FCSTD DOCUMENT  (FreeCAD 0.14R3702 (Git))
Label: flipped_right_side_plate
License: CC-BY 3.0
LicenseURL: http://creativecommons.org/licenses/by/3.0/
objects: Part::Feature×34, Mesh::Feature×23, Part::Cylinder×15, Sketcher::SketchObject×4, PartDesign::Pocket×4, Part::Box×2
note: 63 computed .brp shape members not serialized (recipe doc carries the construction recipe); baked Part::Feature solids carry a one-line shape summary decoded from their .brp

FEATURE [Part::Cylinder] Cylinder  label="left_back_rod"
  Angle = 360
  Height = 1200
  Placement = pos=(-480,-780,-10) rot=(0,0,1;0rad)
  Radius = 4
FEATURE [Part::Cylinder] Cylinder001  label="right_back_rod"
  Angle = 360
  Height = 1200
  Placement = pos=(480,-780,-10) rot=(0,0,1;0rad)
  Radius = 4
FEATURE [Part::Cylinder] Cylinder002  label="right_front_rod"
  Angle = 360
  Height = 1200
  Placement = pos=(480,-938,-10) rot=(0,0,1;0rad)
  Radius = 4
FEATURE [Part::Cylinder] Cylinder003  label="left_front_rod"
  Angle = 360
  Height = 1200
  Placement = pos=(-480,-938,-10) rot=(0,0,-1;1.5708rad)
  Radius = 4
FEATURE [Part::Feature] Part__Feature023  label="left_stepper_motor"
  Placement = pos=(-471,-867,-13) rot=(0,0,1;0rad)
  shape: bbox 48 x 42.3 x 60.1 mm, 110 faces (baked)
FEATURE [Part::Feature] Part__Feature025  label="right_stepper_motor"
  Placement = pos=(471,-867,-13) rot=(0,0,1;0rad)
  shape: bbox 48 x 42.3 x 60.1 mm, 110 faces (baked)
FEATURE [Part::Feature] Part__Feature027  label="left_front_bottom_guide"
  Placement = pos=(-500,-938,-5) rot=(0,0,-1;1.5708rad)
  shape: bbox 32.8 x 42 x 14 mm, 11 faces (baked)
FEATURE [Part::Feature] Part__Feature028  label="left_front_top_guide"
  Placement = pos=(-500,-938,1045) rot=(0,0,-1;1.5708rad)
  shape: bbox 32.8 x 42 x 14 mm, 11 faces (baked)
FEATURE [Part::Feature] Part__Feature029  label="left_back_top_guide"
  Placement = pos=(-500,-780,1045) rot=(0,0,-1;1.5708rad)
  shape: bbox 32.8 x 42 x 14 mm, 11 faces (baked)
FEATURE [Part::Feature] Part__Feature030  label="left_back_bottom_guide"
  Placement = pos=(-500,-780,-5) rot=(0,0,-1;1.5708rad)
  shape: bbox 32.8 x 42 x 14 mm, 11 faces (baked)
FEATURE [Part::Feature] Part__Feature031  label="right_back_bottom_guide"
  Placement = pos=(500,-780,-5) rot=(0,0,1;1.5708rad)
  shape: bbox 32.8 x 42 x 14 mm, 11 faces (baked)
FEATURE [Part::Feature] Part__Feature032  label="right_front_bottom_guide"
  Placement = pos=(500,-938,-5) rot=(0,0,1;1.5708rad)
  shape: bbox 32.8 x 42 x 14 mm, 11 faces (baked)
FEATURE [Part::Feature] Part__Feature033  label="right_front_top_guide"
  Placement = pos=(500,-938,1045) rot=(0,0,1;1.5708rad)
  shape: bbox 32.8 x 42 x 14 mm, 11 faces (baked)
FEATURE [Part::Feature] Part__Feature034  label="right_back_top_guide"
  Placement = pos=(500,-780,1045) rot=(0,0,1;1.5708rad)
  shape: bbox 32.8 x 42 x 14 mm, 11 faces (baked)
FEATURE [Part::Feature] Part__Feature036  label="left_front_foot"
  Placement = pos=(-510,-975,-45) rot=(0,0,1;0rad)
  shape: bbox 34.53 x 34.53 x 32.52 mm, 61 faces (baked)
FEATURE [Part::Feature] Part__Feature037  label="left_back_foot"
  Placement = pos=(-510,10,-45) rot=(0,0,1;0rad)
  shape: bbox 34.53 x 34.53 x 32.52 mm, 61 faces (baked)
FEATURE [Part::Feature] Part__Feature038  label="right_back_foot"
  Placement = pos=(512,3,-45) rot=(0,0,1;0rad)
  shape: bbox 34.53 x 34.53 x 32.52 mm, 61 faces (baked)
FEATURE [Part::Feature] Part__Feature039  label="right_front_foot"
  Placement = pos=(510,-973,-45) rot=(0,0,1;0rad)
  shape: bbox 34.53 x 34.53 x 32.52 mm, 61 faces (baked)
FEATURE [Part::Cylinder] Cylinder004  label="left_lead_screw"
  Angle = 360
  Height = 1066.8
  Placement = pos=(-482,-836,778) rot=(0,1,0;1.5708rad)
  Radius = 5.556
FEATURE [Part::Cylinder] Cylinder005  label="right_lead_screw"
  Angle = 360
  Height = 1219.2
  Placement = pos=(472,-866,55) rot=(0,0,1;0rad)
  Radius = 4.7625
FEATURE [Part::Cylinder] Cylinder006  label="front_rail_guide_rod"
  Angle = 360
  Height = 1000
  Placement = pos=(-500,-913,800) rot=(0,1,0;1.5708rad)
  Radius = 10
FEATURE [Part::Cylinder] Cylinder007  label="back_rail_guide_rod"
  Angle = 360
  Height = 1000
  Placement = pos=(-500,-805,800) rot=(0,1,0;1.5708rad)
  Radius = 10
FEATURE [Part::Feature] Part__Feature046  label="back_bottom_rail"
  Placement = pos=(-500,0,25) rot=(0,1,0;1.5708rad)
  shape: bbox 1000 x 24.5 x 25 mm, 50 faces (baked)
FEATURE [Part::Feature] Part__Feature047  label="rail"
  Placement = pos=(512.5,0,37.5) rot=(0,0,1;0rad)
  shape: bbox 25 x 24.5 x 1000 mm, 50 faces (baked)
FEATURE [Part::Feature] Part__Feature  label="rail001"
  Placement = pos=(512.5,12.5,0) rot=(1,0,0;1.5708rad)
  shape: bbox 25 x 1000 x 24.5 mm, 50 faces (baked)
FEATURE [Part::Feature] Part__Feature048  label="rail002"
  Placement = pos=(512.5,12.5,25) rot=(1,0,0;1.5708rad)
  shape: bbox 25 x 1000 x 24.5 mm, 50 faces (baked)
FEATURE [Part::Feature] Part__Feature049  label="rail003"
  Placement = pos=(-512.5,0,37.5) rot=(0,0,1;0rad)
  shape: bbox 25 x 24.5 x 1000 mm, 50 faces (baked)
FEATURE [Part::Feature] Part__Feature050  label="back_bottom_rail001"
  Placement = pos=(-500,0,1050) rot=(0,1,0;1.5708rad)
  shape: bbox 1000 x 24.5 x 25 mm, 50 faces (baked)
FEATURE [Part::Feature] Part__Feature051  label="back_bottom_rail002"
  Placement = pos=(-500,-975,25) rot=(0,1,0;1.5708rad)
  shape: bbox 1000 x 24.5 x 25 mm, 50 faces (baked)
FEATURE [Part::Feature] Part__Feature052  label="back_bottom_rail003"
  Placement = pos=(-500,-725,1050) rot=(0,1,0;1.5708rad)
  shape: bbox 1000 x 24.5 x 25 mm, 50 faces (baked)
FEATURE [Part::Feature] Part__Feature053  label="rail004"
  Placement = pos=(512.5,12.5,1050) rot=(1,0,0;1.5708rad)
  shape: bbox 25 x 1000 x 24.5 mm, 50 faces (baked)
FEATURE [Part::Feature] Part__Feature054  label="rail005"
  Placement = pos=(512.5,-975,37.5) rot=(0,0,1;0rad)
  shape: bbox 25 x 24.5 x 1000 mm, 50 faces (baked)
FEATURE [Part::Feature] Part__Feature055  label="rail006"
  Placement = pos=(512.5,-725,37.5) rot=(0,0,1;0rad)
  shape: bbox 25 x 24.5 x 1000 mm, 50 faces (baked)
FEATURE [Part::Feature] Part__Feature056  label="rail007"
  Placement = pos=(-512.5,12.5,25) rot=(1,0,0;1.5708rad)
  shape: bbox 25 x 1000 x 24.5 mm, 50 faces (baked)
FEATURE [Part::Feature] Part__Feature057  label="rail008"
  Placement = pos=(-512.5,12.5,0) rot=(1,0,0;1.5708rad)
  shape: bbox 25 x 1000 x 24.5 mm, 50 faces (baked)
FEATURE [Part::Feature] Part__Feature058  label="rail009"
  Placement = pos=(-512.5,12.5,1050) rot=(1,0,0;1.5708rad)
  shape: bbox 25 x 1000 x 24.5 mm, 50 faces (baked)
FEATURE [Part::Feature] Part__Feature059  label="rail010"
  Placement = pos=(-512.5,-725,37.5) rot=(0,0,1;0rad)
  shape: bbox 25 x 24.5 x 1000 mm, 50 faces (baked)
FEATURE [Part::Feature] Part__Feature060  label="rail011"
  Placement = pos=(-512.5,-975,37.5) rot=(0,0,1;0rad)
  shape: bbox 25 x 24.5 x 1000 mm, 50 faces (baked)
FEATURE [Part::Feature] Part__Feature061  label="1"
  Placement = pos=(-472,-867,52) rot=(0,1,0;1.5708rad)
  shape: bbox 20 x 20 x 28 mm, 505 faces (baked)
FEATURE [Part::Feature] Part__Feature062  label="002"
  Placement = pos=(470,-867,52) rot=(0,1,0;1.5708rad)
  shape: bbox 20 x 20 x 28 mm, 505 faces (baked)
FEATURE [Part::Cylinder] Cylinder008  label="Cylinder"
  Angle = 360
  Height = 7
  Placement = pos=(-471,-866,80) rot=(0,0,1;0rad)
  Radius = 11
FEATURE [Part::Cylinder] Cylinder010  label="x-axis-bearing-left"
  Angle = 360
  Height = 9
  Placement = pos=(-453,-836,778) rot=(0,1,0;1.5708rad)
  Radius = 15
FEATURE [Part::Cylinder] Cylinder012  label="left_lead_screw001"
  Angle = 360
  Height = 1219.2
  Placement = pos=(-472,-866,55) rot=(0,0,1;0rad)
  Radius = 4.7625
FEATURE [Part::Cylinder] Cylinder014  label="x-axis-bearing-right"
  Angle = 360
  Height = 9
  Placement = pos=(466,-836,778) rot=(0,1,0;1.5708rad)
  Radius = 15
FEATURE [Part::Cylinder] Cylinder015  label="Cylinder006"
  Angle = 360
  Height = 7
  Placement = pos=(471,-866,80) rot=(0,0,1;0rad)
  Radius = 11
FEATURE [Part::Cylinder] Cylinder016  label="Cylinder007"
  Angle = 360
  Height = 7
  Placement = pos=(471,-866,1053) rot=(0,0,1;0rad)
  Radius = 11
FEATURE [Part::Cylinder] Cylinder017  label="Cylinder008"
  Angle = 360
  Height = 7
  Placement = pos=(-471,-866,1053) rot=(0,0,1;0rad)
  Radius = 11
FEATURE [Part::Feature] Part__Feature063  label="003"
  Placement = pos=(-477,-835,779) rot=(0,0,1;0rad)
  shape: bbox 28 x 20 x 20 mm, 505 faces (baked)
FEATURE [Part::Feature] Part__Feature064  label="x_axis_stepper_motor"
  Placement = pos=(-541,-835,779) rot=(0,1,0;1.5708rad)
  shape: bbox 60.1 x 42.3 x 48 mm, 110 faces (baked)
FEATURE [Mesh::Feature] top_bearing_mount_lr  label="top_bearing_mount_left"
  Placement = pos=(-494,-826,1062.5) rot=(0.707107,-0.707107,0;3.14159rad)
FEATURE [Mesh::Feature] top_bearing_mount_lr001  label="top_bearing_mount_right"
  Placement = pos=(494,-906,1062.5) rot=(0.707107,0.707107,0;3.14159rad)
FEATURE [Sketcher::SketchObject] Sketch
  Placement = pos=(-453,-836,778) rot=(0.707107,0,-0.707107;3.14159rad)
  Support = -> Cylinder010 [Face3]
  sketch-geometry (1):
    g0: Circle CenterX=0 CenterY=0 CenterZ=0 NormalX=0 NormalY=0 NormalZ=1 Radius=5
  constraints (2):
    c: Coincident(g0,g-1)
    c: Radius(g0) = 5
FEATURE [PartDesign::Pocket] Pocket
  Length = 5
  Placement = pos=(-453,-836,778) rot=(0,1,0;1.5708rad)
  Sketch = -> Sketch
  Type = 1
FEATURE [Sketcher::SketchObject] Sketch001
  Placement = pos=(466,-836,778) rot=(0.707107,0,-0.707107;3.14159rad)
  Support = -> Cylinder014 [Face3]
  sketch-geometry (1):
    g0: Circle CenterX=0 CenterY=0 CenterZ=0 NormalX=0 NormalY=0 NormalZ=1 Radius=5
  constraints (2):
    c: Radius(g0) = 5
    c: Coincident(g0,g-1)
FEATURE [PartDesign::Pocket] Pocket001
  Length = 5
  Placement = pos=(466,-836,778) rot=(0,1,0;1.5708rad)
  Sketch = -> Sketch001
  Type = 1
FEATURE [Part::Box] Box  label="left_slide_rail_plate"
  Height = 80
  Length = 6
  Placement = pos=(493,-958,759) rot=(0,0,1;0rad)
  Width = 200
FEATURE [Mesh::Feature] lm8uu_bearing
  Placement = pos=(480,-780,760) rot=(0,0,1;0rad)
FEATURE [Sketcher::SketchObject] Sketch002
  Placement = pos=(499,-958,759) rot=(0.57735,0.57735,0.57735;2.0944rad)
  Support = -> Box [Face2]
  sketch-geometry (24):
    g0: Circle CenterX=45 CenterY=41 CenterZ=0 NormalX=0 NormalY=0 NormalZ=1 Radius=10
    g1: Circle CenterX=153 CenterY=41 CenterZ=0 NormalX=0 NormalY=0 NormalZ=1 Radius=10
    g2: Circle CenterX=122 CenterY=19 CenterZ=0 NormalX=0 NormalY=0 NormalZ=1 Radius=10
    g3: Circle CenterX=36.5 CenterY=74 CenterZ=0 NormalX=0 NormalY=0 NormalZ=1 Radius=2.5
    g4: Circle CenterX=36.5 CenterY=60 CenterZ=0 NormalX=0 NormalY=0 NormalZ=1 Radius=2.5
    g5: Circle CenterX=5.5 CenterY=74 CenterZ=0 NormalX=0 NormalY=0 NormalZ=1 Radius=2.5
    g6: Circle CenterX=5.5 CenterY=60 CenterZ=0 NormalX=0 NormalY=0 NormalZ=1 Radius=2.5
    g7: Circle CenterX=37 CenterY=19.5 CenterZ=0 NormalX=0 NormalY=0 NormalZ=1 Radius=2.5
    g8: Circle CenterX=37 CenterY=5.5 CenterZ=0 NormalX=0 NormalY=0 NormalZ=1 Radius=2.5
    g9: Circle CenterX=5.5 CenterY=19.5 CenterZ=0 NormalX=0 NormalY=0 NormalZ=1 Radius=2.5
    g10: Circle CenterX=5.5 CenterY=5.5 CenterZ=0 NormalX=0 NormalY=0 NormalZ=1 Radius=2.5
    g11: Circle CenterX=162.5 CenterY=19.5 CenterZ=0 NormalX=0 NormalY=0 NormalZ=1 Radius=2.5
    g12: Circle CenterX=162.5 CenterY=5.5 CenterZ=0 NormalX=0 NormalY=0 NormalZ=1 Radius=2.5
    g13: Circle CenterX=194 CenterY=19.5 CenterZ=0 NormalX=0 NormalY=0 NormalZ=1 Radius=2.5
    g14: Circle CenterX=194 CenterY=5.5 CenterZ=0 NormalX=0 NormalY=0 NormalZ=1 Radius=2.5
    g15: Circle CenterX=162.5 CenterY=74 CenterZ=0 NormalX=0 NormalY=0 NormalZ=1 Radius=2.5
    g16: Circle CenterX=162.5 CenterY=60 CenterZ=0 NormalX=0 NormalY=0 NormalZ=1 Radius=2.5
    g17: Circle CenterX=194 CenterY=74 CenterZ=0 NormalX=0 NormalY=0 NormalZ=1 Radius=2.5
    g18: Circle CenterX=194 CenterY=60 CenterZ=0 NormalX=0 NormalY=0 NormalZ=1 Radius=2.5
    g19: Circle CenterX=107 CenterY=34 CenterZ=0 NormalX=0 NormalY=0 NormalZ=1 Radius=2.5
    g20: Circle CenterX=135 CenterY=36 CenterZ=0 NormalX=0 NormalY=0 NormalZ=1 Radius=2.5
    g21: Circle CenterX=142 CenterY=10 CenterZ=0 NormalX=0 NormalY=0 NormalZ=1 Radius=2.5
    g22: Circle CenterX=77 CenterY=34 CenterZ=0 NormalX=0 NormalY=0 NormalZ=1 Radius=2.5
    g23: Circle CenterX=77 CenterY=14 CenterZ=0 NormalX=0 NormalY=0 NormalZ=1 Radius=2.5
  constraints (68):
    c: Radius(g0) = 10
    c: DistanceX(g-1,g0) = 45
    c: DistanceY(g-1,g0) = 41
    c: Radius(g1) = 10
    c: DistanceX(g-1,g1) = 153
    c: DistanceY(g-1,g1) = 41
    c: Radius(g2) = 10
    c: DistanceX(g-1,g2) = 122
    c: DistanceY(g-1,g2) = 19
    c: Radius(g3) = 2.5
    c: DistanceX(g-1,g3) = 36.5
    c: Equal(g4,g3)
    c: DistanceX(g-1,g4) = 36.5
    c: DistanceY(g-1,g4) = 60
    c: Equal(g4,g5)
    c: DistanceX(g5) = 5.5
    c: DistanceX(g6) = 5.5
    c: DistanceY(g-1,g6) = 60
    c: Equal(g5,g6)
    c: Equal(g6,g9)
    c: Equal(g9,g10)
    c: Equal(g10,g7)
    c: Equal(g7,g8)
    c: Equal(g8,g22)
    c: Equal(g22,g23)
    c: Equal(g23,g19)
    c: Equal(g20,g21)
    c: Equal(g21,g11)
    c: Equal(g11,g12)
    c: Equal(g12,g15)
    c: Equal(g15,g16)
    c: Equal(g16,g17)
    c: Equal(g17,g18)
    c: Equal(g18,g13)
    c: Equal(g13,g14)
    c: DistanceX(g-1,g9) = 5.5
    c: DistanceX(g-1,g10) = 5.5
    c: DistanceX(g7,g9) = -31.5
    c: DistanceX(g8,g10) = -31.5
    c: DistanceY(g9,g10) = -14
    c: DistanceY(g7,g8) = -14
    c: DistanceY(g-1,g8) = 5.5
    c: DistanceY(g-1,g10) = 5.5
    c: DistanceY(g12,g11) = 14
    c: DistanceY(g13,g14) = -14
    c: DistanceY(g-1,g12) = 5.5
    c: DistanceY(g-1,g14) = 5.5
    c: DistanceX(g-1,g11) = 162.5
    c: DistanceX(g-1,g12) = 162.5
    c: DistanceX(g12,g14) = 31.5
    c: DistanceX(g11,g13) = 31.5
    c: DistanceY(g16,g15) = 14
    c: DistanceY(g17,g18) = -14
    c: DistanceX(g16,g18) = 31.5
    c: DistanceX(g15,g17) = 31.5
    c: DistanceX(g-1,g16) = 162.5
    c: DistanceX(g-1,g15) = 162.5
    c: DistanceY(g-1,g16) = 60
    c: DistanceY(g-1,g18) = 60
    c: DistanceY(g-1,g21) = 10
    c: DistanceX(g-1,g21) = 142
    c: DistanceX(g-1,g20) = 135
    c: DistanceY(g21,g20) = 26
    c: DistanceX(g-1,g19) = 107
    c: DistanceY(g-1,g23) = 14
    c: DistanceY(g23,g22) = 20
    c: DistanceX(g19,g22) = -30
    c: DistanceY(g-1,g19) = 34
FEATURE [Mesh::Feature] lm8uu_bearing001
  Placement = pos=(480,-780,813) rot=(0,0,1;0rad)
FEATURE [Mesh::Feature] lm8uu_bearing002
  Placement = pos=(480,-938,760) rot=(0,0,1;0rad)
FEATURE [Mesh::Feature] lm8uu_bearing003
  Placement = pos=(480,-938,814) rot=(0,0,1;0rad)
FEATURE [PartDesign::Pocket] Pocket002
  Length = 5
  Placement = pos=(493,-958,759) rot=(0,0,1;0rad)
  Sketch = -> Sketch002
  Type = 1
FEATURE [Mesh::Feature] lead_screw_flange  label="x-axis-lead-screw-flange"
  Placement = pos=(0,-836,778) rot=(0,1,0;1.5708rad)
FEATURE [Mesh::Feature] lead_screw_flange001  label="z-axis-lead-screw-flange-right"
  Placement = pos=(472,-866,721) rot=(0,0,1;0rad)
FEATURE [Mesh::Feature] lead_screw_flange002  label="z-axis-lead-screw-flange-left"
  Placement = pos=(-472,-866,721) rot=(0,0,-1;0.523599rad)
FEATURE [Part::Box] Box001  label="Cube001"
  Height = 80
  Length = 6
  Placement = pos=(-460,-958,759) rot=(0,0,1;0rad)
  Width = 200
FEATURE [Sketcher::SketchObject] Sketch003
  Placement = pos=(-454,-958,759) rot=(0.57735,0.57735,0.57735;2.0944rad)
  Support = -> Box001 [Face2]
  sketch-geometry (24):
    g0: Circle CenterX=45 CenterY=41 CenterZ=0 NormalX=0 NormalY=0 NormalZ=1 Radius=10
    g1: Circle CenterX=153 CenterY=41 CenterZ=0 NormalX=0 NormalY=0 NormalZ=1 Radius=10
    g2: Circle CenterX=122 CenterY=19 CenterZ=0 NormalX=0 NormalY=0 NormalZ=1 Radius=10
    g3: Circle CenterX=36.5 CenterY=74 CenterZ=0 NormalX=0 NormalY=0 NormalZ=1 Radius=2.5
    g4: Circle CenterX=36.5 CenterY=60 CenterZ=0 NormalX=0 NormalY=0 NormalZ=1 Radius=2.5
    g5: Circle CenterX=5.5 CenterY=74 CenterZ=0 NormalX=0 NormalY=0 NormalZ=1 Radius=2.5
    g6: Circle CenterX=5.5 CenterY=60 CenterZ=0 NormalX=0 NormalY=0 NormalZ=1 Radius=2.5
    g7: Circle CenterX=37 CenterY=19.5 CenterZ=0 NormalX=0 NormalY=0 NormalZ=1 Radius=2.5
    g8: Circle CenterX=37 CenterY=5.5 CenterZ=0 NormalX=0 NormalY=0 NormalZ=1 Radius=2.5
    g9: Circle CenterX=5.5 CenterY=19.5 CenterZ=0 NormalX=0 NormalY=0 NormalZ=1 Radius=2.5
    g10: Circle CenterX=5.5 CenterY=5.5 CenterZ=0 NormalX=0 NormalY=0 NormalZ=1 Radius=2.5
    g11: Circle CenterX=162.5 CenterY=19.5 CenterZ=0 NormalX=0 NormalY=0 NormalZ=1 Radius=2.5
    g12: Circle CenterX=162.5 CenterY=5.5 CenterZ=0 NormalX=0 NormalY=0 NormalZ=1 Radius=2.5
    g13: Circle CenterX=194 CenterY=19.5 CenterZ=0 NormalX=0 NormalY=0 NormalZ=1 Radius=2.5
    g14: Circle CenterX=194 CenterY=5.5 CenterZ=0 NormalX=0 NormalY=0 NormalZ=1 Radius=2.5
    g15: Circle CenterX=162.5 CenterY=74 CenterZ=0 NormalX=0 NormalY=0 NormalZ=1 Radius=2.5
    g16: Circle CenterX=162.5 CenterY=60 CenterZ=0 NormalX=0 NormalY=0 NormalZ=1 Radius=2.5
    g17: Circle CenterX=194 CenterY=74 CenterZ=0 NormalX=0 NormalY=0 NormalZ=1 Radius=2.5
    g18: Circle CenterX=194 CenterY=60 CenterZ=0 NormalX=0 NormalY=0 NormalZ=1 Radius=2.5
    g19: Circle CenterX=107 CenterY=34 CenterZ=0 NormalX=0 NormalY=0 NormalZ=1 Radius=2.5
    g20: Circle CenterX=135 CenterY=36 CenterZ=0 NormalX=0 NormalY=0 NormalZ=1 Radius=2.5
    g21: Circle CenterX=142 CenterY=10 CenterZ=0 NormalX=0 NormalY=0 NormalZ=1 Radius=2.5
    g22: Circle CenterX=77 CenterY=34 CenterZ=0 NormalX=0 NormalY=0 NormalZ=1 Radius=2.5
    g23: Circle CenterX=77 CenterY=14 CenterZ=0 NormalX=0 NormalY=0 NormalZ=1 Radius=2.5
  constraints (68):
    c: Radius(g0) = 10
    c: DistanceX(g-1,g0) = 45
    c: DistanceY(g-1,g0) = 41
    c: Radius(g1) = 10
    c: DistanceX(g-1,g1) = 153
    c: DistanceY(g-1,g1) = 41
    c: Radius(g2) = 10
    c: DistanceX(g-1,g2) = 122
    c: DistanceY(g-1,g2) = 19
    c: Radius(g3) = 2.5
    c: DistanceX(g-1,g3) = 36.5
    c: Equal(g4,g3)
    c: DistanceX(g-1,g4) = 36.5
    c: DistanceY(g-1,g4) = 60
    c: Equal(g4,g5)
    c: DistanceX(g5) = 5.5
    c: DistanceX(g6) = 5.5
    c: DistanceY(g-1,g6) = 60
    c: Equal(g5,g6)
    c: Equal(g6,g9)
    c: Equal(g9,g10)
    c: Equal(g10,g7)
    c: Equal(g7,g8)
    c: Equal(g8,g22)
    c: Equal(g22,g23)
    c: Equal(g23,g19)
    c: Equal(g20,g21)
    c: Equal(g21,g11)
    c: Equal(g11,g12)
    c: Equal(g12,g15)
    c: Equal(g15,g16)
    c: Equal(g16,g17)
    c: Equal(g17,g18)
    c: Equal(g18,g13)
    c: Equal(g13,g14)
    c: DistanceX(g-1,g9) = 5.5
    c: DistanceX(g-1,g10) = 5.5
    c: DistanceX(g7,g9) = -31.5
    c: DistanceX(g8,g10) = -31.5
    c: DistanceY(g9,g10) = -14
    c: DistanceY(g7,g8) = -14
    c: DistanceY(g-1,g8) = 5.5
    c: DistanceY(g-1,g10) = 5.5
    c: DistanceY(g12,g11) = 14
    c: DistanceY(g13,g14) = -14
    c: DistanceY(g-1,g12) = 5.5
    c: DistanceY(g-1,g14) = 5.5
    c: DistanceX(g-1,g11) = 162.5
    c: DistanceX(g-1,g12) = 162.5
    c: DistanceX(g12,g14) = 31.5
    c: DistanceX(g11,g13) = 31.5
    c: DistanceY(g16,g15) = 14
    c: DistanceY(g17,g18) = -14
    c: DistanceX(g16,g18) = 31.5
    c: DistanceX(g15,g17) = 31.5
    c: DistanceX(g-1,g16) = 162.5
    c: DistanceX(g-1,g15) = 162.5
    c: DistanceY(g-1,g16) = 60
    c: DistanceY(g-1,g18) = 60
    c: DistanceY(g-1,g21) = 10
    c: DistanceX(g-1,g21) = 142
    c: DistanceX(g-1,g20) = 135
    c: DistanceY(g21,g20) = 26
    c: DistanceX(g-1,g19) = 107
    c: DistanceY(g-1,g23) = 14
    c: DistanceY(g23,g22) = 20
    c: DistanceX(g19,g22) = -30
    c: DistanceY(g-1,g19) = 34
FEATURE [PartDesign::Pocket] Pocket003
  Length = 5
  Placement = pos=(-460,-958,759) rot=(0,0,1;0rad)
  Sketch = -> Sketch003
  Type = 1
FEATURE [Mesh::Feature] slide_rail_flange_mount  label="slide_rail_flange_mount_right"
  Placement = pos=(1000,-119,165) rot=(0.57735,0.57735,0.57735;2.0944rad)
FEATURE [Mesh::Feature] slide_rail_flange_mount001  label="slide_rail_flange_mount_left"
  Placement = pos=(80,-119,165) rot=(0.57735,0.57735,0.57735;2.0944rad)
FEATURE [Mesh::Feature] nema_17_mount  label="nema_17_mount_right"
  Placement = pos=(500,-890,32) rot=(0.57735,0.57735,-0.57735;4.18879rad)
FEATURE [Mesh::Feature] nema_17_mount001  label="nema_17_mount_left"
  Placement = pos=(-500,-846,32) rot=(0.57735,-0.57735,0.57735;4.18879rad)
FEATURE [Mesh::Feature] sc20uu
  Placement = pos=(99,-805,800) rot=(0.707107,0.707107,0;3.14159rad)
FEATURE [Mesh::Feature] sc20uu001
  Placement = pos=(-90,-805,800) rot=(0.707107,0.707107,0;3.14159rad)
FEATURE [Mesh::Feature] sc20uu002
  Placement = pos=(-90,-913,800) rot=(0.707107,0.707107,0;3.14159rad)
FEATURE [Mesh::Feature] sc20uu003
  Placement = pos=(99,-912,800) rot=(0.707107,0.707107,0;3.14159rad)
FEATURE [Mesh::Feature] ArmMountSlidePlate
  Placement = pos=(194,-951,821) rot=(0,0,1;1.5708rad)
FEATURE [Mesh::Feature] NEMA_17_Stepper_Mount
  Placement = pos=(-460,-836,779) rot=(0.707107,0,-0.707107;3.14159rad)
FEATURE [Mesh::Feature] lm8uu_round_split_xnaron001  label="lm8uu-round-split-xnaron001"
  Placement = pos=(469,-760,813) rot=(0,0,-1;1.5708rad)
FEATURE [Mesh::Feature] lm8uu_round_split_xnaron  label="lm8uu-round-split-xnaron002"
  Placement = pos=(469,-918,813) rot=(0,0,-1;1.5708rad)
FEATURE [Mesh::Feature] lm8uu_round_split_xnaron002  label="lm8uu-round-split-xnaron003"
  Placement = pos=(469,-918,760) rot=(0,0,-1;1.5708rad)
FEATURE [Mesh::Feature] lm8uu_round_split_xnaron003  label="lm8uu-round-split-xnaron004"
  Placement = pos=(469,-760,760) rot=(0,0,-1;1.5708rad)
